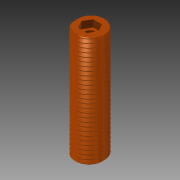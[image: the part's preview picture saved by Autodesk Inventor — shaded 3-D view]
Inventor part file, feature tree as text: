
AUTODESK INVENTOR PART (.ipt)
format: ipt  version: 2013 (Build 170138000, 138)  size: 464,384 bytes
history: native  units: mm
features: sketch x3, extrude x2, helix x1, projected_geometry x1
ambient origin geometry x8: Origin, YZ Plane, XZ Plane, XY Plane, X Axis, Y Axis, Z Axis, Center Point
bodies: Solid1 (feature_tree)
feature tree (7):
  extrude  "Extrusion1"  Depth=5.0mm
  helix  "Coil1"  [1 undecoded]
  extrude  "Extrusion2"  Depth=7.5mm
  sketch  "Sketch1"  dims[d0=14.5mm d2=5.0mm d3=55.0mm d4=0.0mm]
  sketch  "Sketch2"  dims[d5=2.0mm]
  sketch  "Sketch3"  dims[d6=2.001mm d7=10.0mm d8=300.0mm d9=0.0mm d10=90.0deg d11=90.0deg d12=0.0mm d13=0.0mm d14=7.5mm d15=3.5mm d16=0.0mm]
  projected_geometry  "Project Cut Edges1"
note: 1 required parameter value undecoded (feature->parameter linkage not recoverable at this tier; creation-order binding heuristic only, values carry confidence <= 0.55)
